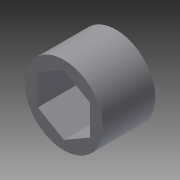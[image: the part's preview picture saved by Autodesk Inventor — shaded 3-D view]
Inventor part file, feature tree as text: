
AUTODESK INVENTOR PART (.ipt)
format: ipt  version: 2013 (Build 170138000, 138)  size: 80,384 bytes
history: native  units: in
note: dims shown in document units (in); Inventor stores cm internally (conversion verified against a paired STEP export)
features: extrude x1, sketch x1
ambient origin geometry x8: Origin, YZ Plane, XZ Plane, XY Plane, X Axis, Y Axis, Z Axis, Center Point
bodies: Solid1 (feature_tree)
feature tree (2):
  extrude  "Extrusion1"  Depth=0.5in
  sketch  "Sketch1"  dims[d0=0.75in d1=0.5in d2=0.5in d3=0.0in]
